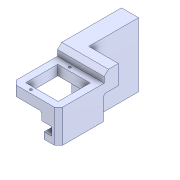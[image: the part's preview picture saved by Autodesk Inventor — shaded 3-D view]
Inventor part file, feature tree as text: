
AUTODESK INVENTOR PART (.ipt)
format: ipt  version: 2020 (Build 240168000, 168)  size: 142,336 bytes
history: mixed  units: mm
features: extrude x2, sketch x2, other x1, imported_body x1
ambient origin geometry x8: Origin, YZ Plane, XZ Plane, XY Plane, X Axis, Y Axis, Z Axis, Center Point
bodies: Solid1 (imported_parasolid)
feature tree (6):
  extrude  "Extrusion1"  Depth=24.0mm TaperAngle=0.0deg
  extrude  "Extrusion2"  [1 undecoded]
  sketch  "Sketch1"  dims[d0=25.0mm d1=0.0mm d2=24.0mm d3=0.0mm]
  sketch  "Sketch2"
  other  "Cut-Extrude3"
  imported_body  NMx_Import_Brep_tag  [imported B-rep: ~40 faces, bbox_mm=[32.8, 45.14, 77.1]]
note: 1 required parameter value undecoded (feature->parameter linkage not recoverable at this tier; creation-order binding heuristic only, values carry confidence <= 0.55)
